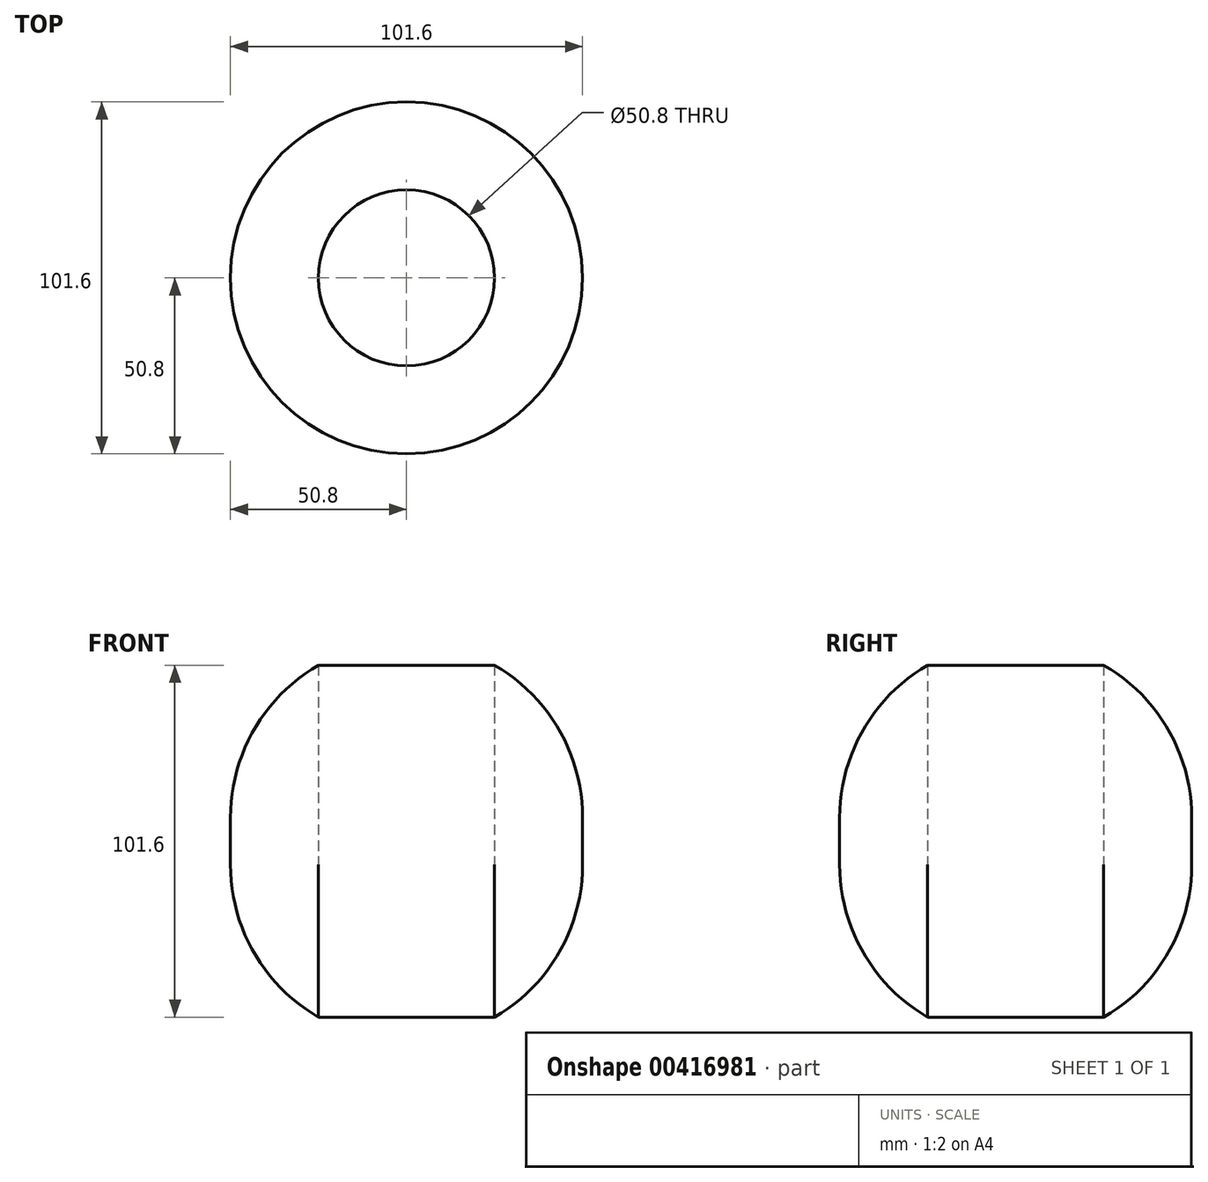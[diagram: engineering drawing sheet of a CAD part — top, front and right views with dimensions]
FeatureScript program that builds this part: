
annotation { "Feature Type Name" : "Feature", "Feature Type Description" : "" }
export const myFeature = defineFeature(function(context is Context, id is Id, definition is map)
    precondition{}
    {
        {
            var Q0;
            Q0=qCreatedBy(makeId("Top.planeOp"),FACE);
            var sketch = newSketch(context, id + "F0", { "sketchPlane" : qUnion([Q0])});
            skCircle(sketch, "E0", {"center": v(0, 0) * mm, "radius": 50.8 * mm});
            skSolve(sketch);
        }
        {
            var Q0;
            Q0=makeQuery(id+"F0.imprint","IMPRINT",FACE,{"disambiguationData":[TD([[makeQuery(id+"F0.imprint","IMPRINT",EDGE,{"derivedFrom":sQuery(id+"F0.wireOp",EDGE,"E0")}),1.0]])]});
            var sketch = newSketch(context, id + "F1", { "sketchPlane" : qUnion([Q0])});
            skCircle(sketch, "E1", {"center": v(0, 0) * mm, "radius": 25.4 * mm});
            skSolve(sketch);
        }
        {
            var Q0;
            Q0 = qSketchRegion(id + "F1", true);
            extrude(context, id + "F2", {"entities" : qUnion([Q0]), "depth" : 101.6 * mm});
        }
        {
            var Q0;
            Q0=makeQuery(id+"F0.imprint","IMPRINT",FACE,{"disambiguationData":[TD([[makeQuery(id+"F0.imprint","IMPRINT",EDGE,{"derivedFrom":sQuery(id+"F0.wireOp",EDGE,"E0")}),1.0]])]});
            extrude(context, id + "F3", {"entities" : qUnion([Q0]), "operationType" : NewBodyOperationType.ADD, "depth" : 101.6 * mm});
        }
        {
            var Q0;
            Q0=makeQuery(id+"F3.boolean.opBoolean","MERGE",FACE,{"derivedFrom":[makeQuery(id+"F2.opExtrude","CAP_FACE",FACE,{"disambiguationData":[OSD([sQuery(id+"F1.wireOp",EDGE,"E1")])],"isStart":true}),makeQuery(id+"F3.opExtrude","CAP_FACE",FACE,{"disambiguationData":[OSD([sQuery(id+"F0.wireOp",EDGE,"E0")])],"isStart":true})]});
            var sketch = newSketch(context, id + "F4", { "sketchPlane" : qUnion([Q0])});
            skCircle(sketch, "E2", {"center": v(0, 0) * mm, "radius": 25.4 * mm});
            skSolve(sketch);
        }
        {
            var Q0;
            Q0=makeQuery(id+"F4.imprint","IMPRINT",FACE,{"disambiguationData":[TD([[makeQuery(id+"F4.imprint","IMPRINT",EDGE,{"derivedFrom":sQuery(id+"F4.wireOp",EDGE,"E2")}),1.0]])]});
            extrude(context, id + "F5", {"entities" : qUnion([Q0]), "operationType" : NewBodyOperationType.REMOVE, "endBound" : BoundingType.THROUGH_ALL, "oppositeDirection" : true, "depth" : 25.4 * mm});
        }
        {
            var Q0;
            Q0=makeQuery(id+"F3.opExtrude","CAP_EDGE",EDGE,{"disambiguationData":[OSD([sQuery(id+"F0.wireOp",EDGE,"E0")])],"isStart":false});
            var Q1;
            Q1=makeQuery(id+"F3.opExtrude","CAP_EDGE",EDGE,{"disambiguationData":[OSD([sQuery(id+"F0.wireOp",EDGE,"E0")])],"isStart":true});
            fillet(context, id + "F6", {"entities" : qUnion([Q0, Q1]), "radius" : 50.8 * mm, "tangentPropagation" : true, "allowEdgeOverflow" : false});
        }
    });
